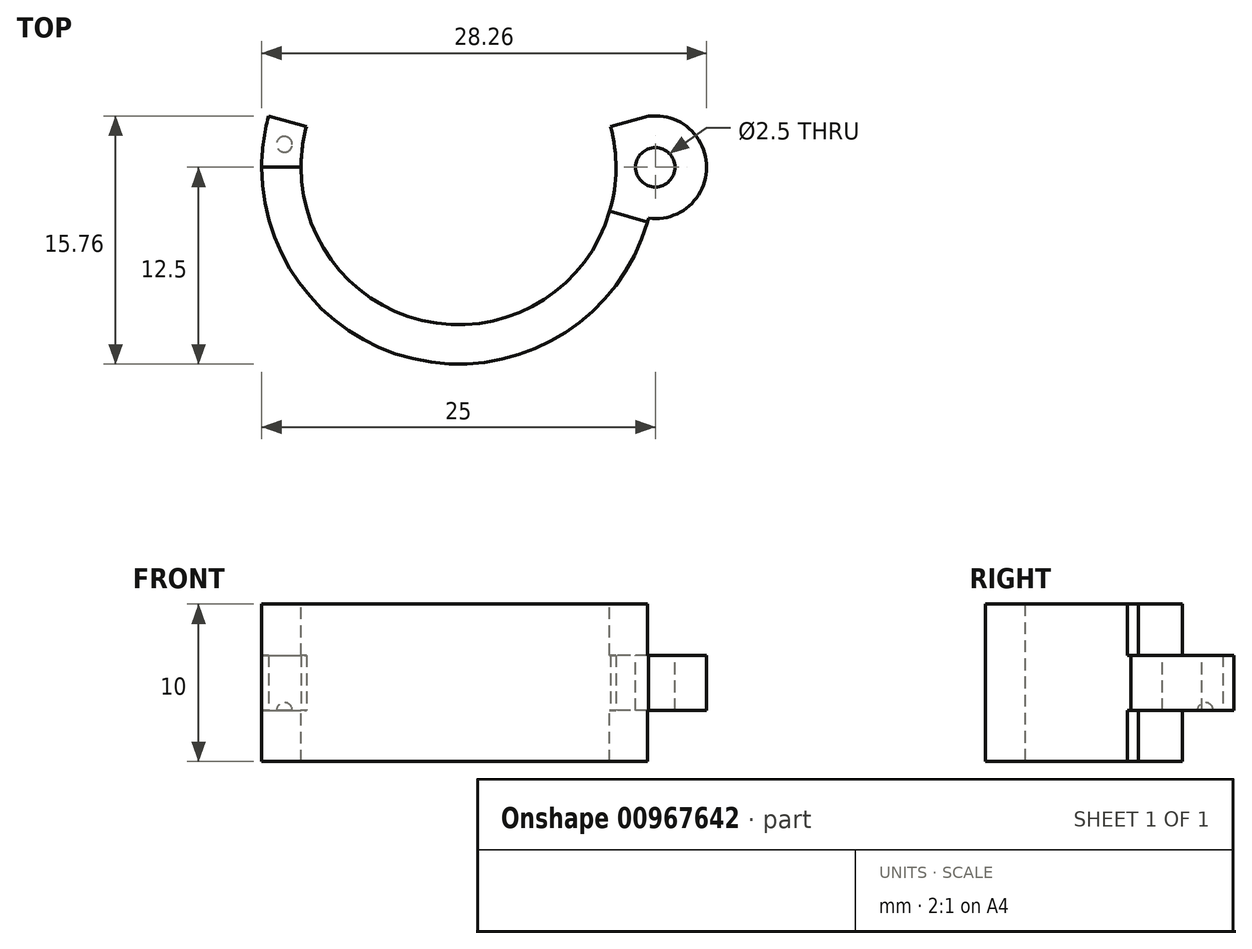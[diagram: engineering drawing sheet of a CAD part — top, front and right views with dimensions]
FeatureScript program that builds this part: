
annotation { "Feature Type Name" : "Feature", "Feature Type Description" : "" }
export const myFeature = defineFeature(function(context is Context, id is Id, definition is map)
    precondition{}
    {
        {
            var Q0;
            Q0=qCreatedBy(makeId("Top.planeOp"),FACE);
            var sketch = newSketch(context, id + "F0", { "sketchPlane" : qUnion([Q0])});
            skArc(sketch, "E0", {"start": v(-9.66, 2.59) * mm, "mid": v(0, -10) * mm, "end": v(9.66, 2.59) * mm});
            skArc(sketch, "E1", {"start": v(-12.07, 3.24) * mm, "mid": v(0, -12.5) * mm, "end": v(12.07, 3.24) * mm});
            skLineSegment(sketch, "E2", {"start": v(0, 12.5) * mm, "end": v(0, -12.5) * mm, "construction": true});
            skLineSegment(sketch, "E3", {"start": v(-10, 0) * mm, "end": v(12.5, 0) * mm, "construction": true});
            skLineSegment(sketch, "E4", {"start": v(0, 0) * mm, "end": v(12.07, 3.24) * mm, "construction": true});
            skLineSegment(sketch, "E5", {"start": v(0, 0) * mm, "end": v(12.07, -3.24) * mm, "construction": true});
            skArc(sketch, "E6", {"start": v(12.07, -3.24) * mm, "mid": v(15.76, 0) * mm, "end": v(12.07, 3.24) * mm});
            skLineSegment(sketch, "E7", {"start": v(12.07, 3.24) * mm, "end": v(9.66, 2.59) * mm});
            skLineSegment(sketch, "E8", {"start": v(0, 0) * mm, "end": v(-12.07, 3.24) * mm, "construction": true});
            skPoint(sketch, "E9.start.orphan", {"position": v(-12.5, 0) * mm});
            skLineSegment(sketch, "E10", {"start": v(-12.07, 3.24) * mm, "end": v(-9.66, 2.59) * mm});
            skSolve(sketch);
        }
        {
            var Q0;
            Q0 = qSketchRegion(id + "F0", true);
            extrude(context, id + "F1", {"entities" : qUnion([Q0]), "depth" : 3.5 * mm, "offsetDistance" : 25 * mm});
        }
        {
            var Q0;
            Q0=makeQuery(id+"F1.opExtrude","CAP_FACE",FACE,{"disambiguationData":[OSD([sQuery(id+"F0.wireOp",EDGE,"E0"),sQuery(id+"F0.wireOp",EDGE,"E1"),sQuery(id+"F0.wireOp",EDGE,"E6"),sQuery(id+"F0.wireOp",EDGE,"E7"),sQuery(id+"F0.wireOp",EDGE,"E9")])],"isStart":false});
            var sketch = newSketch(context, id + "F2", { "sketchPlane" : qUnion([Q0])});
            skCircle(sketch, "E11", {"center": v(12.5, 0) * mm, "radius": 1.25 * mm});
            skSolve(sketch);
        }
        {
            var Q0;
            Q0 = qSketchRegion(id + "F2", true);
            var Q1;
            Q1=makeQuery(id+"F1.opExtrude","CAP_FACE",FACE,{"disambiguationData":[OSD([sQuery(id+"F0.wireOp",EDGE,"E0"),sQuery(id+"F0.wireOp",EDGE,"E1"),sQuery(id+"F0.wireOp",EDGE,"E6"),sQuery(id+"F0.wireOp",EDGE,"E7"),sQuery(id+"F0.wireOp",EDGE,"E9")])],"isStart":true});
            extrude(context, id + "F3", {"entities" : qUnion([Q0]), "operationType" : NewBodyOperationType.REMOVE, "endBound" : BoundingType.UP_TO_SURFACE, "oppositeDirection" : true, "depth" : 25 * mm, "endBoundEntityFace" : qUnion([Q1]), "offsetDistance" : 25 * mm});
        }
        {
            var Q0;
            Q0=makeQuery(id+"F1.opExtrude","CAP_FACE",FACE,{"disambiguationData":[OSD([sQuery(id+"F0.wireOp",EDGE,"E0"),sQuery(id+"F0.wireOp",EDGE,"E1"),sQuery(id+"F0.wireOp",EDGE,"E6"),sQuery(id+"F0.wireOp",EDGE,"E7"),sQuery(id+"F0.wireOp",EDGE,"E10")])],"isStart":true});
            var sketch = newSketch(context, id + "F4", { "sketchPlane" : qUnion([Q0])});
            skLineSegment(sketch, "E12", {"start": v(-12.5, 0) * mm, "end": v(-10, 0) * mm});
            skArc(sketch, "E13", {"start": v(12.07, 3.24) * mm, "mid": v(10.8, 2.79) * mm, "end": v(9.82, 1.87) * mm, "construction": true});
            skPoint(sketch, "E14", {"position": v(12.07, 3.24) * mm});
            skPoint(sketch, "E15", {"position": v(9.82, 1.87) * mm});
            skArc(sketch, "E16.0", {"start": v(12, 3.48) * mm, "mid": v(10.76, 3.05) * mm, "end": v(9.76, 2.2) * mm, "construction": true});
            skLineSegment(sketch, "E17", {"start": v(12, 3.48) * mm, "end": v(9.6, 2.78) * mm});
            skSolve(sketch);
        }
        {
            var Q0;
            {var subQ0=sQuery(id+"F4.wireOp",EDGE,"E12");Q0=makeQuery(id+"F4.imprint","IMPRINT",FACE,{"disambiguationData":[TD([[makeQuery(id+"F4.imprint","IMPRINT",EDGE,{"derivedFrom":subQ0}),1.0]])]});}
            extrude(context, id + "F5", {"entities" : qUnion([Q0]), "operationType" : NewBodyOperationType.ADD, "depth" : 3.25 * mm, "offsetDistance" : 25 * mm, "hasSecondDirection" : true, "secondDirectionOppositeDirection" : true, "secondDirectionDepth" : 6.75 * mm});
        }
        {
            var Q0;
            {var subQ0=sQuery(id+"F0.wireOp",EDGE,"E10");var subQ1=sQuery(id+"F0.wireOp",EDGE,"E1");var subQ2=sQuery(id+"F0.wireOp",EDGE,"E0");Q0=makeQuery(id+"F5.boolean.opBoolean","SPLIT",FACE,{"disambiguationData":[TD([makeQuery(id+"F1.opExtrude","SWEPT_FACE",FACE,{"disambiguationData":[OSD([subQ0])]})])],"derivedFrom":makeQuery(id+"F1.opExtrude","CAP_FACE",FACE,{"disambiguationData":[OSD([subQ2,subQ1,sQuery(id+"F0.wireOp",EDGE,"E6"),sQuery(id+"F0.wireOp",EDGE,"E7"),subQ0])],"isStart":true})});}
            var sketch = newSketch(context, id + "F6", { "sketchPlane" : qUnion([Q0])});
            skLineSegment(sketch, "E18", {"start": v(-10.87, -2.91) * mm, "end": v(-11.25, 0) * mm, "construction": true});
            skLineSegment(sketch, "E19", {"start": v(-12.4, -1.63) * mm, "end": v(-9.91, -1.3) * mm, "construction": true});
            skArc(sketch, "E20", {"start": v(-11.12, -0.96) * mm, "mid": v(-11.55, -1.52) * mm, "end": v(-11, -1.95) * mm});
            skLineSegment(sketch, "E21", {"start": v(-11, -1.95) * mm, "end": v(-11.12, -0.96) * mm});
            skSolve(sketch);
        }
        {
            var Q0;
            Q0=makeQuery(id+"F6.imprint","IMPRINT",FACE,{"disambiguationData":[TD([[makeQuery(id+"F6.imprint","IMPRINT",EDGE,{"derivedFrom":sQuery(id+"F6.wireOp",EDGE,"E20")}),1.0]])]});
            var Q1;
            Q1=sQuery(id+"F6.wireOp",EDGE,"E21");
            revolve(context, id + "F7", {"operationType" : NewBodyOperationType.REMOVE, "surfaceOperationType" : NewSurfaceOperationType.NEW, "entities" : qUnion([Q0]), "axis" : qUnion([Q1]), "revolveType" : RevolveType.FULL, "oppositeDirection" : true});
        }
    });
